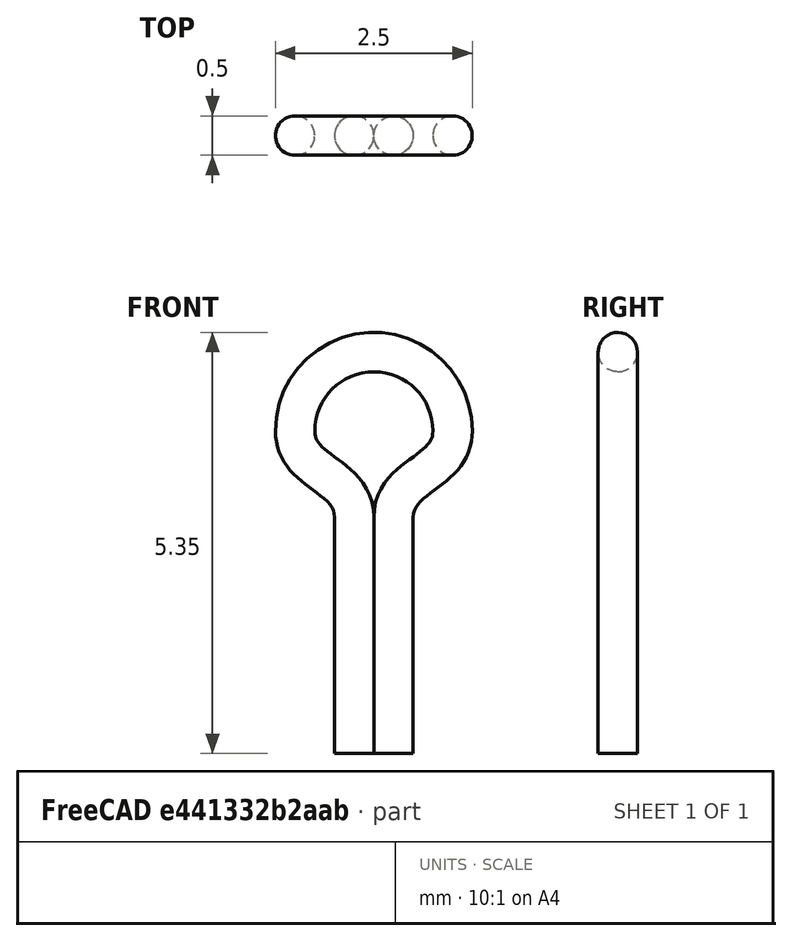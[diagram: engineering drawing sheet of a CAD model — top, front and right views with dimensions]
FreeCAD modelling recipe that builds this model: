
FCSTD DOCUMENT  (FreeCAD 0.17R12018 (Git))
Label: Test_Point_Loop_D2.50mm_Drill1.0mm_LowProfile
License: All rights reserved
LicenseURL: http://en.wikipedia.org/wiki/All_rights_reserved
objects: Sketcher::SketchObject×2, Spreadsheet::Sheet×1, PartDesign::AdditivePipe×1, PartDesign::Body×1, App::Part×1
note: 5 computed .brp shape members not serialized (recipe doc carries the construction recipe); baked Part::Feature solids carry a one-line shape summary decoded from their .brp

FEATURE [Spreadsheet::Sheet] Spreadsheet  label="dims"
  cells = A1="DWire"; B1(DWire)=0.5; A2="DLoop"; B2(DLoop)=2.5; A3="Spacer"; B3(Spacer)=0; A4="DSpacer"; B4(DSpacer)=3; A5="Lall"; B5(Lall)=5.0999999999999996; A6="Ddrill"; B6(Ddrill)=1; A7="Lbottom"; B7(Lbottom)=3
FEATURE [Sketcher::SketchObject] Sketch001
  MapMode = 5
  Placement = pos=(0,0,0) rot=(1,0,0;1.5708rad)
  expr: Constraints[35] = (dims.Ddrill - dims.DWire) / 2
  expr: Constraints[33] = dims.Spacer
  expr: Constraints[31] = dims.Lbottom
  expr: Constraints[34] = dims.Ddrill - dims.DWire
  expr: Constraints[29] = dims.Lall - (dims.DLoop - dims.DWire) / 2
  expr: Constraints[28] = (dims.DLoop - dims.DWire) / 2
  sketch-geometry (25):
    g0: LineSegment StartX=-0.25 StartY=-3 StartZ=0 EndX=-0.25 EndY=-8.3697e-08 EndZ=0
    g1: LineSegment StartX=0.25 StartY=-2.34629e-07 StartZ=0 EndX=0.25 EndY=-3 EndZ=0
    g2: ArcOfCircle CenterX=0 CenterY=1.1 CenterZ=0 NormalX=0 NormalY=0 NormalZ=1 Radius=1 StartAngle=7.9023e-08 EndAngle=3.14159
    g3: LineSegment [constr] StartX=-1 StartY=1.1 StartZ=0 EndX=1 EndY=1.1 EndZ=0
    g4: LineSegment [constr] StartX=-1 StartY=-1.63243e-07 StartZ=0 EndX=1 EndY=-1.63243e-07 EndZ=0
    g5: LineSegment [constr] StartX=1 StartY=1.1 StartZ=0 EndX=1 EndY=-1.63243e-07 EndZ=0
    g6: LineSegment [constr] StartX=-1 StartY=-1.63243e-07 StartZ=0 EndX=-1 EndY=1.1 EndZ=0
    g7: LineSegment [constr] StartX=-0.25 StartY=-8.3697e-08 StartZ=0 EndX=-0.25 EndY=0.549999 EndZ=0
    g8: LineSegment [constr] StartX=0.25 StartY=-2.34629e-07 StartZ=0 EndX=0.25 EndY=0.549999 EndZ=0
    g9: LineSegment [constr] StartX=-1 StartY=0.549999 StartZ=0 EndX=1 EndY=0.549999 EndZ=0
    g10: LineSegment [constr] StartX=0.25 StartY=0.549999 StartZ=0 EndX=0.25 EndY=1.1 EndZ=0
    g11-g14: Circle [constr] x4 (B-spline internal-alignment scaffolding for g15; pole/knot coordinates omitted)
    g15: BSplineCurve PolesCount=4 KnotsCount=2 Degree=3 IsPeriodic=0
    g16: GeomPoint [constr] X=-0.25 Y=-8.3697e-08 Z=0
    g17: GeomPoint [constr] X=-1 Y=1.1 Z=0
    g18-g21: Circle [constr] x4 (B-spline internal-alignment scaffolding for g22; pole/knot coordinates omitted)
    g22: BSplineCurve PolesCount=4 KnotsCount=2 Degree=3 IsPeriodic=0
    g23: GeomPoint [constr] X=0.25 Y=-2.34629e-07 Z=0
    g24: GeomPoint [constr] X=1 Y=1.1 Z=0
  constraints (58):
    c: Vertical(g0)
    c: Vertical(g1)
    c: Coincident(g3,g2)
    c: Horizontal(g3)
    c: PointOnObject(g2,g3)
    c: Coincident(g3,g2)
    c: PointOnObject(g2,g-2)
    c: Horizontal(g4)
    c: Coincident(g5,g2)
    c: Coincident(g5,g4)
    c: Coincident(g6,g4)
    c: Coincident(g6,g2)
    c: PointOnObject(g0,g4)
    c: PointOnObject(g1,g4)
    c: Vertical(g6)
    c: Vertical(g5)
    c: Coincident(g7,g0)
    c: Vertical(g7)
    c: Coincident(g8,g1)
    c: Vertical(g8)
    c: PointOnObject(g9,g6)
    c: PointOnObject(g9,g5)
    c: Horizontal(g9)
    c: PointOnObject(g7,g9)
    c: PointOnObject(g8,g9)
    c: PointOnObject(g10,g3)
    c: Vertical(g10)
    c: Equal(g10,g8)
    c: Radius(g2) = 1
    c: DistanceY(g1,g2) = 4.1
    c: DistanceY(g1,g0) = 0
    c: DistanceY(g0,g-1) = 3
    c: Coincident(g10,g8)
    c: DistanceY(g-1,g0) = 0
    c: DistanceX(g0,g1) = 0.5
    c: DistanceX(g0,g-1) = 0.25
    c: Coincident(g11,g0)
    c: Radius(g11) = 0
    c: Equal(g11,g12)
    c: Coincident(g12,g7)
    c: Equal(g11,g13)
    c: Coincident(g13,g9)
    c: Equal(g11,g14)
    c: Coincident(g14,g2)
    c: InternalAlignment(g11-g14 -> g15) x4
    c: InternalAlignment(g16,g15)
    c: InternalAlignment(g17,g15)
    c: Coincident(g18,g1)
    c: Radius(g18) = 0
    c: Equal(g18,g19)
    c: Coincident(g19,g8)
    c: Equal(g18,g20)
    c: Coincident(g20,g9)
    c: Equal(g18,g21)
    c: Coincident(g21,g2)
    c: InternalAlignment(g18-g21 -> g22) x4
    c: InternalAlignment(g23,g22)
    c: InternalAlignment(g24,g22)
FEATURE [Sketcher::SketchObject] Sketch
  MapMode = 5
  Placement = pos=(0,0,-3) rot=(0,0,1;0rad)
  expr: Constraints[2] = (dims.Ddrill - dims.DWire) / 2
  expr: Constraints[1] = dims.DWire / 2
  sketch-geometry (1):
    g0: Circle CenterX=-0.25 CenterY=0 CenterZ=0 NormalX=0 NormalY=0 NormalZ=1 Radius=0.25
  constraints (3):
    c: PointOnObject(g0,g-1)
    c: Radius(g0) = 0.25
    c: DistanceX(g0,g-1) = 0.25
FEATURE [PartDesign::AdditivePipe] AdditivePipe
  AuxilleryCurvelinear = true
  AuxillerySpineTangent = false
  Binormal = (0,0,0)
  Mode = 0
  Placement = pos=(0,0,-3) rot=(0,0,1;0rad)
  Profile = -> Sketch
  Spine = -> Sketch001 [Edge1,Edge2,Edge3,Edge4,Edge5]
  SpineTangent = false
  Transformation = 0
  Transition = 0
FEATURE [PartDesign::Body] Body  label="Test_Point_Loop_D2.50mm_Drill1.0mm_LowProfile"
  Group = -> [Sketch,Sketch001,AdditivePipe]
  Origin = -> Origin002
  Tip = -> AdditivePipe
FEATURE [App::Part] Part  label="group"
  Group = -> [Body]
  License = CC BY 3.0
  LicenseURL = http://creativecommons.org/licenses/by/3.0/
  Origin = -> Origin
